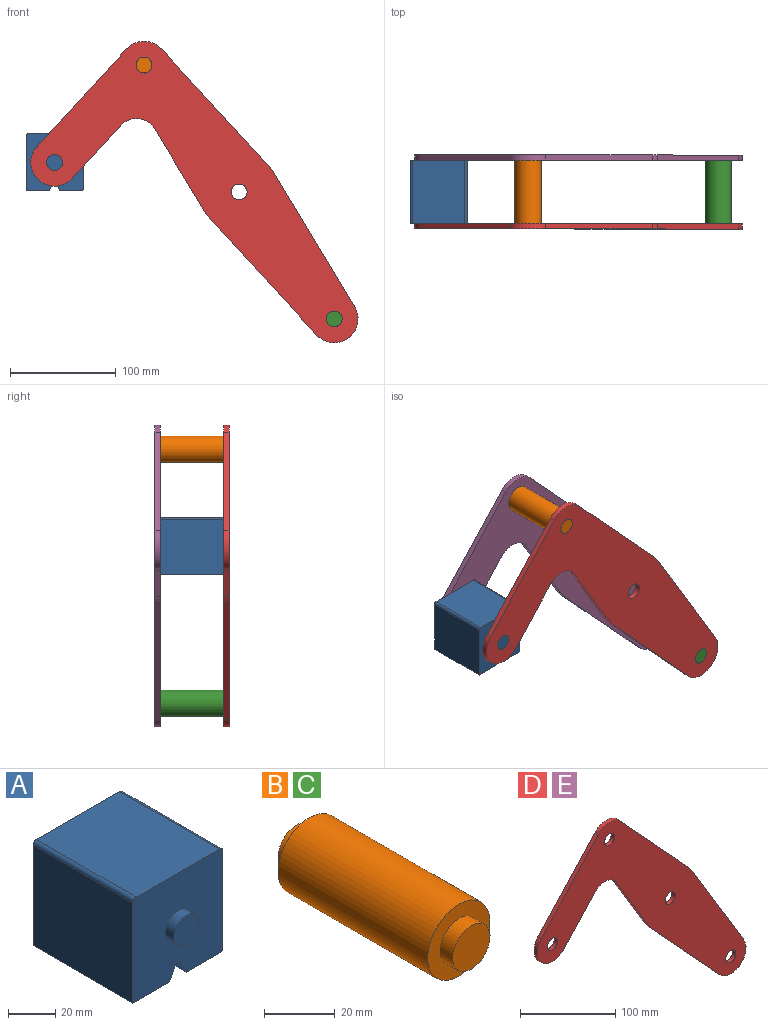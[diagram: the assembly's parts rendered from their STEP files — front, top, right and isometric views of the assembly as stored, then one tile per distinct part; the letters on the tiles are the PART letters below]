
ASSEMBLY  parts=5 mates=3
PART A: 17 faces, bbox 54x70x54 mm
  f0: plane 60x6.42mm, normal (0.89,0,-0.45), area 430.8mm2, adj f1,f4,f10,f13
  f1: plane 60x22mm, normal (0,0,-1), area 1320.2mm2, adj f0,f2,f4,f10
  f2: plane 60x52.01mm, normal (-1,0,0), area 3120.4mm2, adj f1,f4,f10,f14
  f3: plane 60x50.01mm, normal (0,0,1), area 3000.4mm2, adj f4,f10,f14,f15
  f4: plane 54.01x54.01mm, normal (0,-1,0), area 2691mm2, adj f0,f1,f2,f3,f5,f6,f7,f9
  f5: plane 60x50.01mm, normal (1,0,0), area 3000.4mm2, adj f4,f10,f15,f16
  f6: plane 60x6.42mm, normal (-0.89,0,-0.45), area 430.8mm2, adj f4,f7,f10,f13
  f7: plane 60x20mm, normal (0,0,-1), area 1200.2mm2, adj f4,f6,f10,f16
  f8: plane 15x15mm, normal (0,-1,0), area 176.7mm2, adj f9
  f9: cylinder r=7.5mm len=15mm, axis (0,1,0), area 235.6mm2, adj f4,f8
  f10: plane 54.01x54.01mm, normal (0,1,0), area 2691mm2, adj f0,f1,f2,f3,f5,f6,f7,f12
  f11: plane 15x15mm, normal (0,1,0), area 176.7mm2, adj f12
  f12: cylinder r=7.5mm len=15mm, axis (0,-1,0), area 235.6mm2, adj f10,f11
  f13: cylinder r=2mm len=60mm, axis (0,-1,0), area 265.7mm2, adj f0,f4,f6,f10
  f14: cylinder r=2mm len=60mm, axis (0,-1,0), area 188.5mm2, adj f2,f3,f4,f10
  f15: cylinder r=2mm len=60mm, axis (0,1,0), area 188.5mm2, adj f3,f4,f5,f10
  f16: cylinder r=2mm len=60mm, axis (0,-1,0), area 188.5mm2, adj f4,f5,f7,f10
PART B: 7 faces, bbox 25x70x25 mm
  f0: cylinder r=12.5mm len=60mm, axis (0,-1,0), area 4712.4mm2, adj f2,f5
  f1: cylinder r=7.5mm len=15mm, axis (0,1,0), area 235.6mm2, adj f2,f3
  f2: plane 25x25mm, normal (0,-1,0), area 314.2mm2, adj f0,f1
  f3: plane 15x15mm, normal (0,-1,0), area 176.7mm2, adj f1
  f4: cylinder r=7.5mm len=15mm, axis (0,-1,0), area 235.6mm2, adj f5,f6
  f5: plane 25x25mm, normal (0,1,0), area 314.2mm2, adj f0,f4
  f6: plane 15x15mm, normal (0,1,0), area 176.7mm2, adj f4
PART C: same geometry as B
PART D: 18 faces, bbox 309.5x5x285.1 mm
  f0: cylinder r=22.5mm len=39.07mm, axis (0,1,0), area 353.4mm2, adj f1,f13,f16,f17
  f1: plane 50.28x46.21mm, normal (0.74,0,-0.68), area 341.4mm2, adj f0,f2,f16,f17
  f2: cylinder r=20mm len=31.85mm, axis (0,1,0), area 185.5mm2, adj f1,f3,f16,f17
  f3: plane 79.23x47.81mm, normal (-0.86,0,-0.52), area 462.7mm2, adj f2,f4,f16,f17
  f4: cylinder r=37.5mm len=6mm, axis (0,1,0), area 37.6mm2, adj f3,f5,f16,f17
  f5: plane 109.88x101mm, normal (-0.74,0,-0.68), area 746.2mm2, adj f4,f6,f16,f17
  f6: cylinder r=22.5mm len=39.07mm, axis (0,1,0), area 330.9mm2, adj f5,f7,f16,f17
  f7: plane 127.78x77.11mm, normal (0.86,0,0.52), area 746.2mm2, adj f6,f8,f16,f17
  f8: cylinder r=37.5mm len=6mm, axis (0,1,0), area 37.6mm2, adj f7,f9,f16,f17
  f9: plane 109.88x101mm, normal (0.74,0,0.68), area 746.2mm2, adj f8,f10,f16,f17
  f10: cylinder r=22.5mm len=33.13mm, axis (0,1,0), area 186.2mm2, adj f9,f13,f16,f17
  f11: cylinder r=7.5mm len=15mm, axis (0,1,0), area 235.6mm2, adj f16,f17
  f12: cylinder r=7.5mm len=15mm, axis (0,1,0), area 235.6mm2, adj f16,f17
  f13: plane 92.03x84.59mm, normal (-0.74,0,0.68), area 625mm2, adj f0,f10,f16,f17
  f14: cylinder r=7.5mm len=15mm, axis (0,1,0), area 235.6mm2, adj f16,f17
  f15: cylinder r=7.5mm len=15mm, axis (0,1,0), area 235.6mm2, adj f16,f17
  f16: plane 309.5x285.07mm, normal (0,-1,0), area 24555.4mm2, adj f0,f1,f2,f3,f4,f5,f6,f7
  f17: plane 309.5x285.07mm, normal (0,1,0), area 24555.4mm2, adj f0,f1,f2,f3,f4,f5,f6,f7
PART E: same geometry as D
PLACE A t=(-11.5,-30.38,-4.78)mm
PLACE B t=(-11.5,-30.38,-4.78)mm
PLACE C t=(168.41,-30.38,-244.85)mm
PLACE D t=(-11.5,-30.38,-4.78)mm fixed
PLACE E t=(-11.5,34.62,-4.78)mm
MATE fastened C.f0 <-> D.f6  axis (0,-1,0) through (78.45,-30.38,-124.81)mm
MATE revolute A.f9 <-> D.f0  axis (0,-1,0) through (-186.05,-30.38,23.22)mm
MATE fastened B.f0 <-> E.f10  axis (0,1,0) through (-101.46,29.62,115.25)mm
